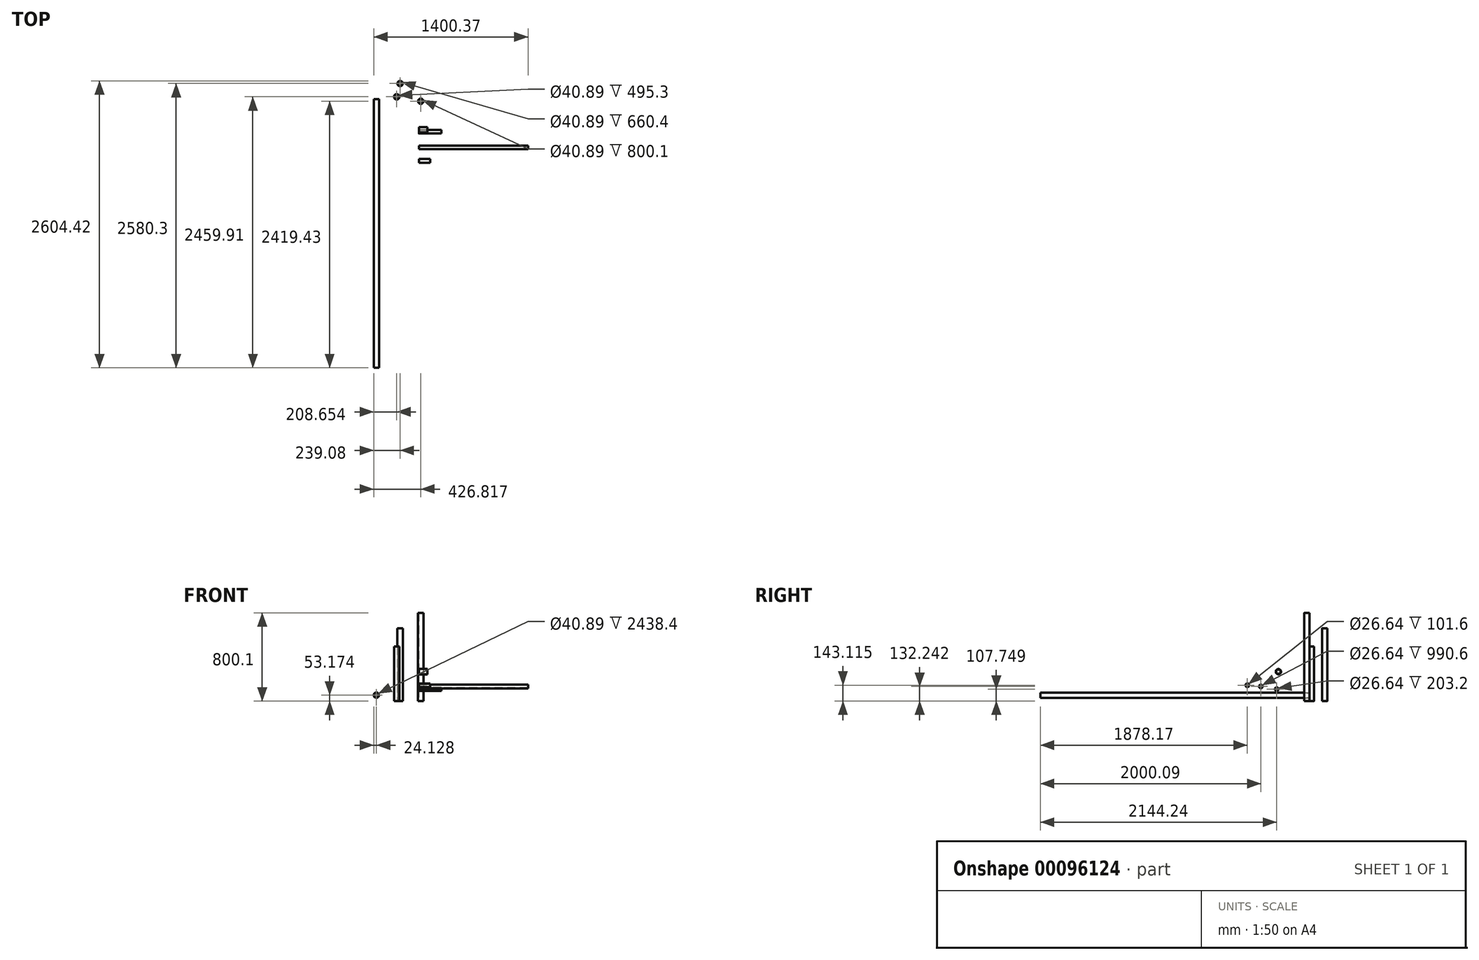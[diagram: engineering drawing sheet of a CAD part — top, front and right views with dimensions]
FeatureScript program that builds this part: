
annotation { "Feature Type Name" : "Feature", "Feature Type Description" : "" }
export const myFeature = defineFeature(function(context is Context, id is Id, definition is map)
    precondition{}
    {
        {
            var Q0;
            Q0=qCreatedBy(makeId("Top.planeOp"),FACE);
            var sketch = newSketch(context, id + "F0", { "sketchPlane" : qUnion([Q0])});
            skCircle(sketch, "E0", {"center": v(17.05, -18.97) * mm, "radius": 24.13 * mm});
            skCircle(sketch, "E1", {"center": v(17.05, -18.97) * mm, "radius": 20.45 * mm});
            skSolve(sketch);
        }
        {
            var Q0;
            Q0=makeQuery(id+"F0.imprint","IMPRINT",FACE,{"disambiguationData":[TD([[makeQuery(id+"F0.imprint","IMPRINT",EDGE,{"derivedFrom":sQuery(id+"F0.wireOp",EDGE,"E0")}),1.0]])]});
            extrude(context, id + "F1", {"entities" : qUnion([Q0]), "depth" : 800.1 * mm});
        }
        {
            var Q0;
            Q0=qCreatedBy(makeId("Top.planeOp"),FACE);
            var sketch = newSketch(context, id + "F2", { "sketchPlane" : qUnion([Q0])});
            skCircle(sketch, "E2", {"center": v(-170.7, 141.9) * mm, "radius": 24.13 * mm});
            skCircle(sketch, "E3", {"center": v(-170.7, 141.9) * mm, "radius": 20.45 * mm});
            skSolve(sketch);
        }
        {
            var Q0;
            Q0=makeQuery(id+"F2.imprint","IMPRINT",FACE,{"disambiguationData":[TD([[makeQuery(id+"F2.imprint","IMPRINT",EDGE,{"derivedFrom":sQuery(id+"F2.wireOp",EDGE,"E2")}),1.0]])]});
            extrude(context, id + "F3", {"entities" : qUnion([Q0]), "depth" : 660.4 * mm});
        }
        {
            var Q0;
            Q0=qCreatedBy(makeId("Top.planeOp"),FACE);
            var sketch = newSketch(context, id + "F4", { "sketchPlane" : qUnion([Q0])});
            skCircle(sketch, "E4", {"center": v(-201.12, 21.51) * mm, "radius": 24.13 * mm});
            skCircle(sketch, "E5", {"center": v(-201.12, 21.51) * mm, "radius": 20.45 * mm});
            skSolve(sketch);
        }
        {
            var Q0;
            Q0=makeQuery(id+"F4.imprint","IMPRINT",FACE,{"disambiguationData":[TD([[makeQuery(id+"F4.imprint","IMPRINT",EDGE,{"derivedFrom":sQuery(id+"F4.wireOp",EDGE,"E4")}),1.0]])]});
            extrude(context, id + "F5", {"entities" : qUnion([Q0]), "depth" : 495.3 * mm});
        }
        {
            var Q0;
            Q0=qCreatedBy(makeId("Right.planeOp"),FACE);
            var sketch = newSketch(context, id + "F6", { "sketchPlane" : qUnion([Q0])});
            skCircle(sketch, "E6", {"center": v(-278.6, 266.24) * mm, "radius": 24.13 * mm});
            skCircle(sketch, "E7", {"center": v(-278.6, 266.24) * mm, "radius": 20.45 * mm});
            skSolve(sketch);
        }
        {
            var Q0;
            Q0=makeQuery(id+"F6.imprint","IMPRINT",FACE,{"disambiguationData":[TD([[makeQuery(id+"F6.imprint","IMPRINT",EDGE,{"derivedFrom":sQuery(id+"F6.wireOp",EDGE,"E6")}),1.0]])]});
            extrude(context, id + "F7", {"entities" : qUnion([Q0]), "depth" : 76.2 * mm});
        }
        {
            var Q0;
            Q0=qCreatedBy(makeId("Right.planeOp"),FACE);
            var sketch = newSketch(context, id + "F8", { "sketchPlane" : qUnion([Q0])});
            skCircle(sketch, "E8", {"center": v(-294.16, 107.75) * mm, "radius": 16.7 * mm});
            skCircle(sketch, "E9", {"center": v(-294.16, 107.75) * mm, "radius": 13.32 * mm});
            skSolve(sketch);
        }
        {
            var Q0;
            Q0=makeQuery(id+"F8.imprint","IMPRINT",FACE,{"disambiguationData":[TD([[makeQuery(id+"F8.imprint","IMPRINT",EDGE,{"derivedFrom":sQuery(id+"F8.wireOp",EDGE,"E8")}),1.0]])]});
            extrude(context, id + "F9", {"entities" : qUnion([Q0]), "depth" : 203.2 * mm});
        }
        {
            var Q0;
            Q0=qCreatedBy(makeId("Right.planeOp"),FACE);
            var sketch = newSketch(context, id + "F10", { "sketchPlane" : qUnion([Q0])});
            skCircle(sketch, "E10", {"center": v(-438.3, 132.24) * mm, "radius": 16.7 * mm});
            skCircle(sketch, "E11", {"center": v(-438.3, 132.24) * mm, "radius": 13.32 * mm});
            skSolve(sketch);
        }
        {
            var Q0;
            Q0=makeQuery(id+"F10.imprint","IMPRINT",FACE,{"disambiguationData":[TD([[makeQuery(id+"F10.imprint","IMPRINT",EDGE,{"derivedFrom":sQuery(id+"F10.wireOp",EDGE,"E10")}),1.0]])]});
            extrude(context, id + "F11", {"entities" : qUnion([Q0]), "depth" : 990.6 * mm});
        }
        {
            var Q0;
            Q0=qCreatedBy(makeId("Right.planeOp"),FACE);
            var sketch = newSketch(context, id + "F12", { "sketchPlane" : qUnion([Q0])});
            skCircle(sketch, "E12", {"center": v(-560.23, 143.12) * mm, "radius": 16.7 * mm});
            skCircle(sketch, "E13", {"center": v(-560.23, 143.12) * mm, "radius": 13.32 * mm});
            skSolve(sketch);
        }
        {
            var Q0;
            Q0=makeQuery(id+"F12.imprint","IMPRINT",FACE,{"disambiguationData":[TD([[makeQuery(id+"F12.imprint","IMPRINT",EDGE,{"derivedFrom":sQuery(id+"F12.wireOp",EDGE,"E12")}),1.0]])]});
            extrude(context, id + "F13", {"entities" : qUnion([Q0]), "depth" : 101.6 * mm});
        }
        {
            var Q0;
            Q0=qCreatedBy(makeId("Front.planeOp"),FACE);
            var sketch = newSketch(context, id + "F14", { "sketchPlane" : qUnion([Q0])});
            skCircle(sketch, "E14", {"center": v(-385.64, 53.17) * mm, "radius": 24.13 * mm});
            skCircle(sketch, "E15", {"center": v(-385.64, 53.17) * mm, "radius": 20.45 * mm});
            skSolve(sketch);
        }
        {
            var Q0;
            Q0=qSketchRegion(id+"F14",true);
            extrude(context, id + "F15", {"entities" : qUnion([Q0]), "depth" : 2438.4 * mm});
        }
    });
